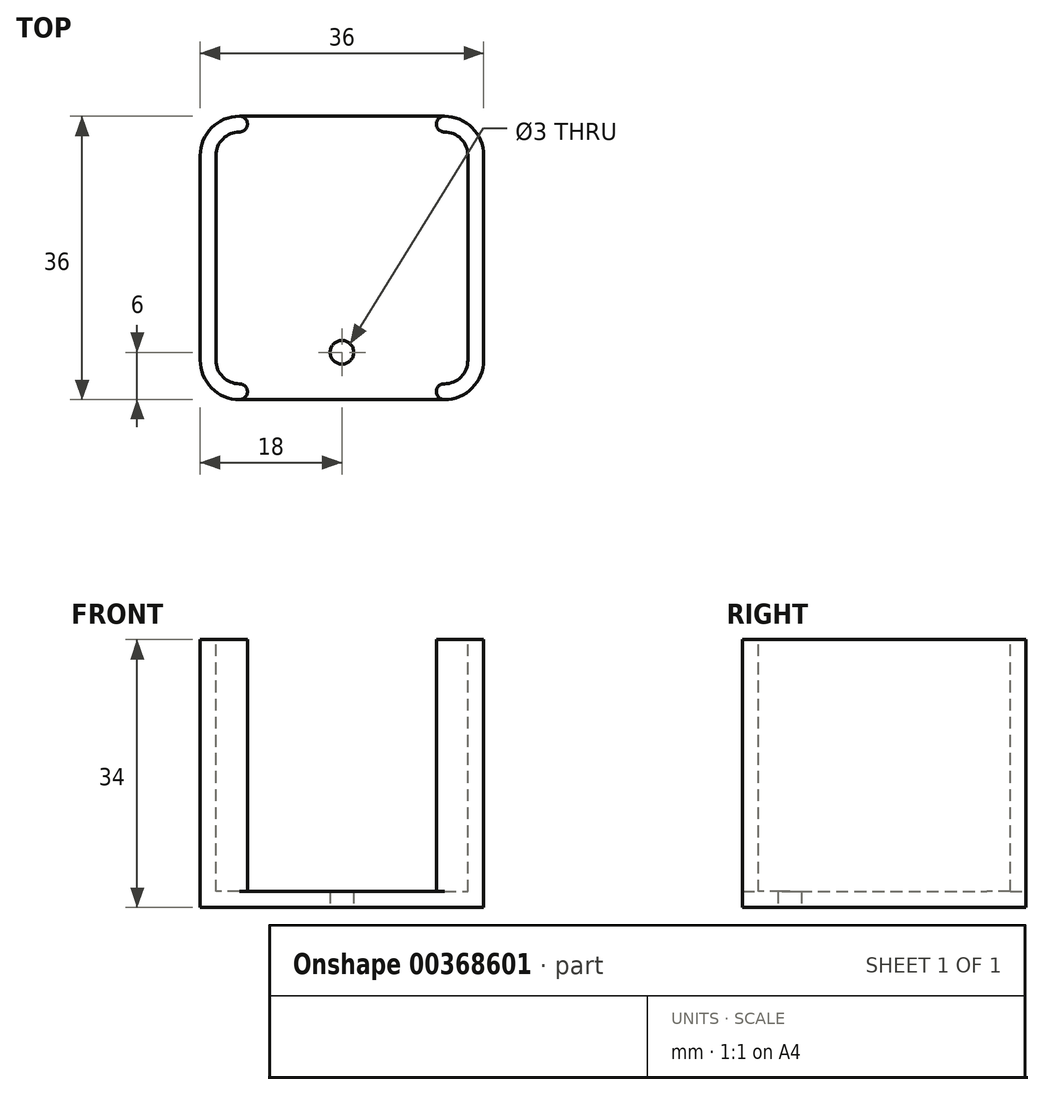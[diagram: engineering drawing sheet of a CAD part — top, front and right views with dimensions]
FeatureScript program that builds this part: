
annotation { "Feature Type Name" : "Feature", "Feature Type Description" : "" }
export const myFeature = defineFeature(function(context is Context, id is Id, definition is map)
    precondition{}
    {
        {
            var Q0;
            Q0=qCreatedBy(makeId("Top.planeOp"),FACE);
            var sketch = newSketch(context, id + "F0", { "sketchPlane" : qUnion([Q0])});
            skLineSegment(sketch, "E0.bottom", {"start": v(18, -18) * mm, "end": v(-18, -18) * mm});
            skLineSegment(sketch, "E0.top", {"start": v(18, 18) * mm, "end": v(-18, 18) * mm});
            skLineSegment(sketch, "E0.left", {"start": v(18, -18) * mm, "end": v(18, 18) * mm});
            skLineSegment(sketch, "E0.right", {"start": v(-18, -18) * mm, "end": v(-18, 18) * mm});
            skPoint(sketch, "E0.middle", {"position": v(0, 0) * mm});
            skSolve(sketch);
        }
        {
            var Q0;
            Q0=makeQuery(id+"F0.imprint","IMPRINT",FACE,{"disambiguationData":[TD([[makeQuery(id+"F0.imprint","IMPRINT",EDGE,{"derivedFrom":sQuery(id+"F0.wireOp",EDGE,"E0.bottom")}),-1.0]])]});
            extrude(context, id + "F1", {"entities" : qUnion([Q0]), "depth" : 34 * mm});
        }
        {
            var Q0;
            Q0=makeQuery(id+"F1.opExtrude","SWEPT_EDGE",EDGE,{"disambiguationData":[OSD([sQuery(id+"F0.wireOp",EDGE,"E0.top"),sQuery(id+"F0.wireOp",EDGE,"E0.left")])]});
            var Q1;
            Q1=makeQuery(id+"F1.opExtrude","SWEPT_EDGE",EDGE,{"disambiguationData":[OSD([sQuery(id+"F0.wireOp",EDGE,"E0.top"),sQuery(id+"F0.wireOp",EDGE,"E0.right")])]});
            var Q2;
            Q2=makeQuery(id+"F1.opExtrude","SWEPT_EDGE",EDGE,{"disambiguationData":[OSD([sQuery(id+"F0.wireOp",EDGE,"E0.bottom"),sQuery(id+"F0.wireOp",EDGE,"E0.left")])]});
            var Q3;
            Q3=makeQuery(id+"F1.opExtrude","SWEPT_EDGE",EDGE,{"disambiguationData":[OSD([sQuery(id+"F0.wireOp",EDGE,"E0.bottom"),sQuery(id+"F0.wireOp",EDGE,"E0.right")])]});
            fillet(context, id + "F2", {"entities" : qUnion([Q0, Q1, Q2, Q3]), "radius" : 5 * mm, "tangentPropagation" : true, "allowEdgeOverflow" : false});
        }
        {
            var Q0;
            Q0=makeQuery(id+"F1.opExtrude","CAP_FACE",FACE,{"disambiguationData":[OSD([sQuery(id+"F0.wireOp",EDGE,"E0.bottom"),sQuery(id+"F0.wireOp",EDGE,"E0.top"),sQuery(id+"F0.wireOp",EDGE,"E0.left"),sQuery(id+"F0.wireOp",EDGE,"E0.right")])],"isStart":false});
            var sketch = newSketch(context, id + "F3", { "sketchPlane" : qUnion([Q0])});
            skArc(sketch, "E1.0", {"start": v(-13, 16) * mm, "mid": v(-15.12, 15.12) * mm, "end": v(-16, 13) * mm});
            skArc(sketch, "E2.0", {"start": v(16, 13) * mm, "mid": v(15.12, 15.12) * mm, "end": v(13, 16) * mm});
            skLineSegment(sketch, "E3.0", {"start": v(16, -13) * mm, "end": v(16, 13) * mm});
            skLineSegment(sketch, "E4.0", {"start": v(-16, -13) * mm, "end": v(-16, 13) * mm});
            skArc(sketch, "E5.0", {"start": v(-16, -13) * mm, "mid": v(-15.12, -15.12) * mm, "end": v(-13, -16) * mm});
            skArc(sketch, "E6.0", {"start": v(13, -16) * mm, "mid": v(15.12, -15.12) * mm, "end": v(16, -13) * mm});
            skLineSegment(sketch, "E7.0", {"start": v(13, -16) * mm, "end": v(-13, -16) * mm});
            skArc(sketch, "E8", {"start": v(-13, 16) * mm, "mid": v(-12, 17) * mm, "end": v(-13, 18) * mm});
            skArc(sketch, "E9", {"start": v(13, 18) * mm, "mid": v(12, 17) * mm, "end": v(13, 16) * mm});
            skSolve(sketch);
        }
        {
            var Q0;
            Q0=makeQuery(id+"F3.imprint","IMPRINT",FACE,{"disambiguationData":[TD([[makeQuery(id+"F3.imprint","IMPRINT",EDGE,{"derivedFrom":sQuery(id+"F3.wireOp",EDGE,"E1.0")}),1.0]])]});
            extrude(context, id + "F4", {"entities" : qUnion([Q0]), "operationType" : NewBodyOperationType.REMOVE, "oppositeDirection" : true, "depth" : 32 * mm});
        }
        {
            var Q0;
            Q0=makeQuery(id+"F1.opExtrude","CAP_FACE",FACE,{"disambiguationData":[OSD([sQuery(id+"F0.wireOp",EDGE,"E0.bottom"),sQuery(id+"F0.wireOp",EDGE,"E0.top"),sQuery(id+"F0.wireOp",EDGE,"E0.left"),sQuery(id+"F0.wireOp",EDGE,"E0.right")])],"isStart":true});
            var sketch = newSketch(context, id + "F5", { "sketchPlane" : qUnion([Q0])});
            skCircle(sketch, "E10", {"center": v(0, 12) * mm, "radius": 1.5 * mm});
            skSolve(sketch);
        }
        {
            var Q0;
            Q0=makeQuery(id+"F5.imprint","IMPRINT",FACE,{"disambiguationData":[TD([[makeQuery(id+"F5.imprint","IMPRINT",EDGE,{"derivedFrom":sQuery(id+"F5.wireOp",EDGE,"E10")}),1.0]])]});
            extrude(context, id + "F6", {"entities" : qUnion([Q0]), "operationType" : NewBodyOperationType.REMOVE, "oppositeDirection" : true, "depth" : 25 * mm});
        }
        {
            var Q0;
            Q0=makeQuery(id+"F1.opExtrude","CAP_FACE",FACE,{"disambiguationData":[OSD([sQuery(id+"F0.wireOp",EDGE,"E0.bottom"),sQuery(id+"F0.wireOp",EDGE,"E0.top"),sQuery(id+"F0.wireOp",EDGE,"E0.left"),sQuery(id+"F0.wireOp",EDGE,"E0.right")])],"isStart":false});
            var sketch = newSketch(context, id + "F7", { "sketchPlane" : qUnion([Q0])});
            skArc(sketch, "E11", {"start": v(-13, -18) * mm, "mid": v(-12, -17) * mm, "end": v(-13, -16) * mm});
            skArc(sketch, "E12", {"start": v(13, -16) * mm, "mid": v(12, -17) * mm, "end": v(13, -18) * mm});
            skSolve(sketch);
        }
        {
            var Q0;
            Q0=makeQuery(id+"F7.imprint","IMPRINT",FACE,{"disambiguationData":[TD([[makeQuery(id+"F7.imprint","IMPRINT",EDGE,{"derivedFrom":sQuery(id+"F7.wireOp",EDGE,"E11")}),-1.0]])]});
            var Q1;
            Q1=makeQuery(id+"F4.boolean.opBoolean","COPY",FACE,{"derivedFrom":makeQuery(id+"F4.opExtrude","CAP_FACE",FACE,{"disambiguationData":[OSD([sQuery(id+"F0.wireOp",EDGE,"E0.top"),sQuery(id+"F3.wireOp",EDGE,"E1.0"),sQuery(id+"F3.wireOp",EDGE,"E2.0"),sQuery(id+"F3.wireOp",EDGE,"E3.0"),sQuery(id+"F3.wireOp",EDGE,"E4.0"),sQuery(id+"F3.wireOp",EDGE,"E5.0"),sQuery(id+"F3.wireOp",EDGE,"E6.0"),sQuery(id+"F3.wireOp",EDGE,"E7.0"),sQuery(id+"F3.wireOp",EDGE,"E8"),sQuery(id+"F3.wireOp",EDGE,"E9")])],"isStart":false})});
            extrude(context, id + "F8", {"entities" : qUnion([Q0]), "operationType" : NewBodyOperationType.REMOVE, "endBound" : BoundingType.UP_TO_SURFACE, "oppositeDirection" : true, "endBoundEntityFace" : qUnion([Q1]), "depth" : 25 * mm});
        }
    });
